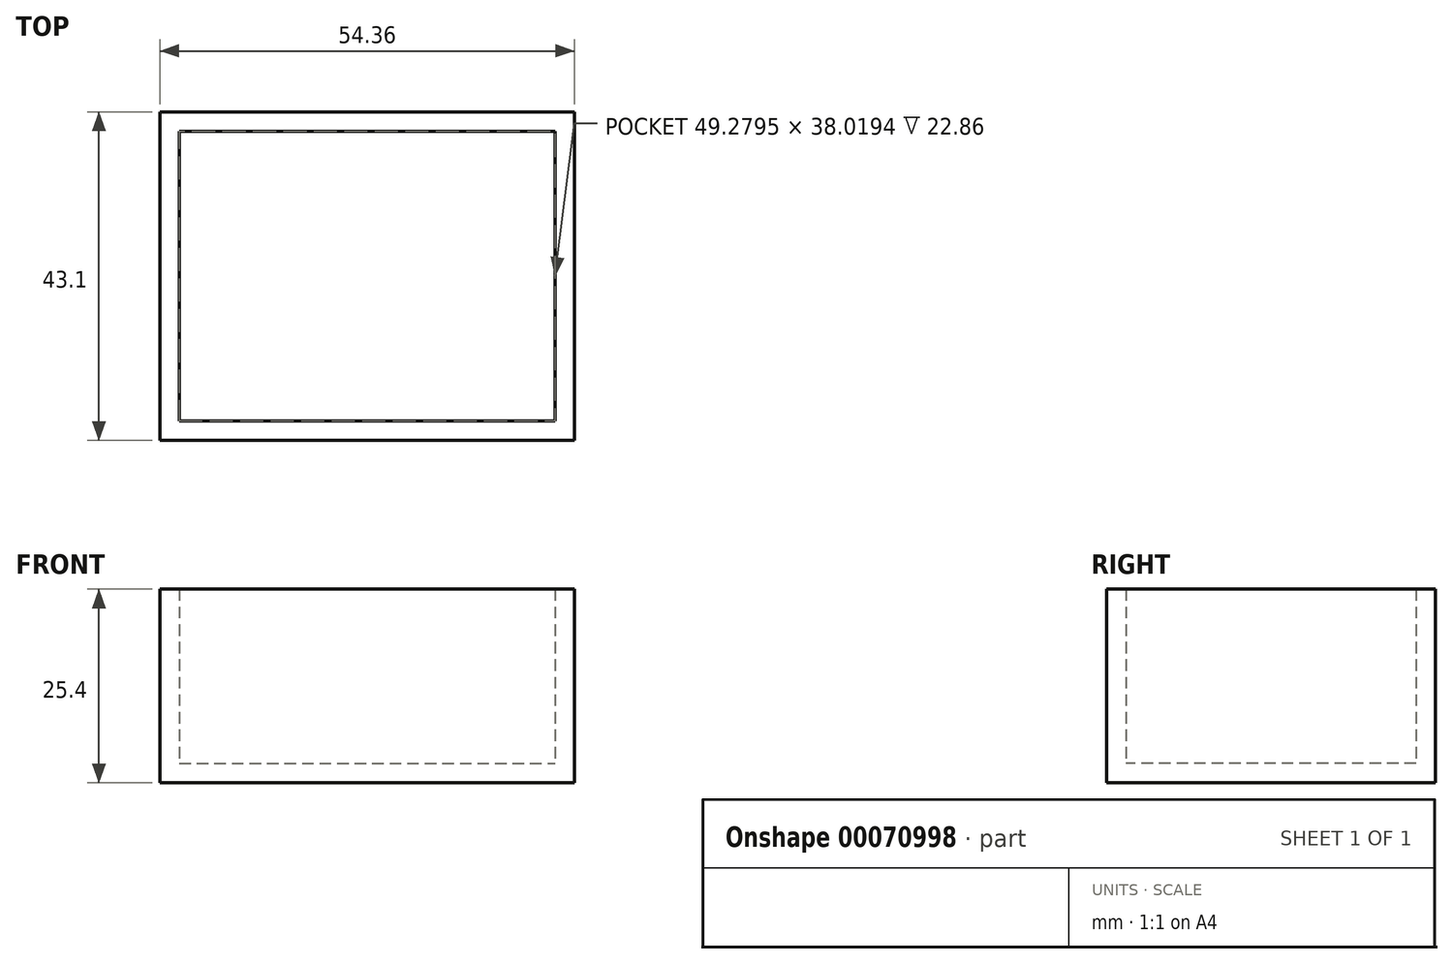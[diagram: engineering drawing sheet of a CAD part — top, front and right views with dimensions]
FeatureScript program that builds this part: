
annotation { "Feature Type Name" : "Feature", "Feature Type Description" : "" }
export const myFeature = defineFeature(function(context is Context, id is Id, definition is map)
    precondition{}
    {
        {
            var Q0;
            Q0=qCreatedBy(makeId("Top.planeOp"),FACE);
            var sketch = newSketch(context, id + "F0", { "sketchPlane" : qUnion([Q0])});
            skLineSegment(sketch, "E0", {"start": v(0, 0) * mm, "end": v(54.36, 0) * mm});
            skLineSegment(sketch, "E1", {"start": v(54.36, 0) * mm, "end": v(54.36, 43.1) * mm});
            skLineSegment(sketch, "E2", {"start": v(54.36, 43.1) * mm, "end": v(0, 43.1) * mm});
            skLineSegment(sketch, "E3", {"start": v(0, 43.1) * mm, "end": v(0, 0) * mm});
            skSolve(sketch);
        }
        {
            var Q0;
            Q0 = qSketchRegion(id + "F0", true);
            extrude(context, id + "F1", {"entities" : qUnion([Q0]), "depth" : 25.4 * mm});
        }
        {
            var Q0;
            Q0=makeQuery(id+"F1.opExtrude","CAP_FACE",FACE,{"disambiguationData":[OSD([sQuery(id+"F0.wireOp",EDGE,"E0"),sQuery(id+"F0.wireOp",EDGE,"E1"),sQuery(id+"F0.wireOp",EDGE,"E2"),sQuery(id+"F0.wireOp",EDGE,"E3")])],"isStart":false});
            shell(context, id + "F2", {"entities" : qUnion([Q0]), "thickness" : 2.54 * mm});
        }
    });
